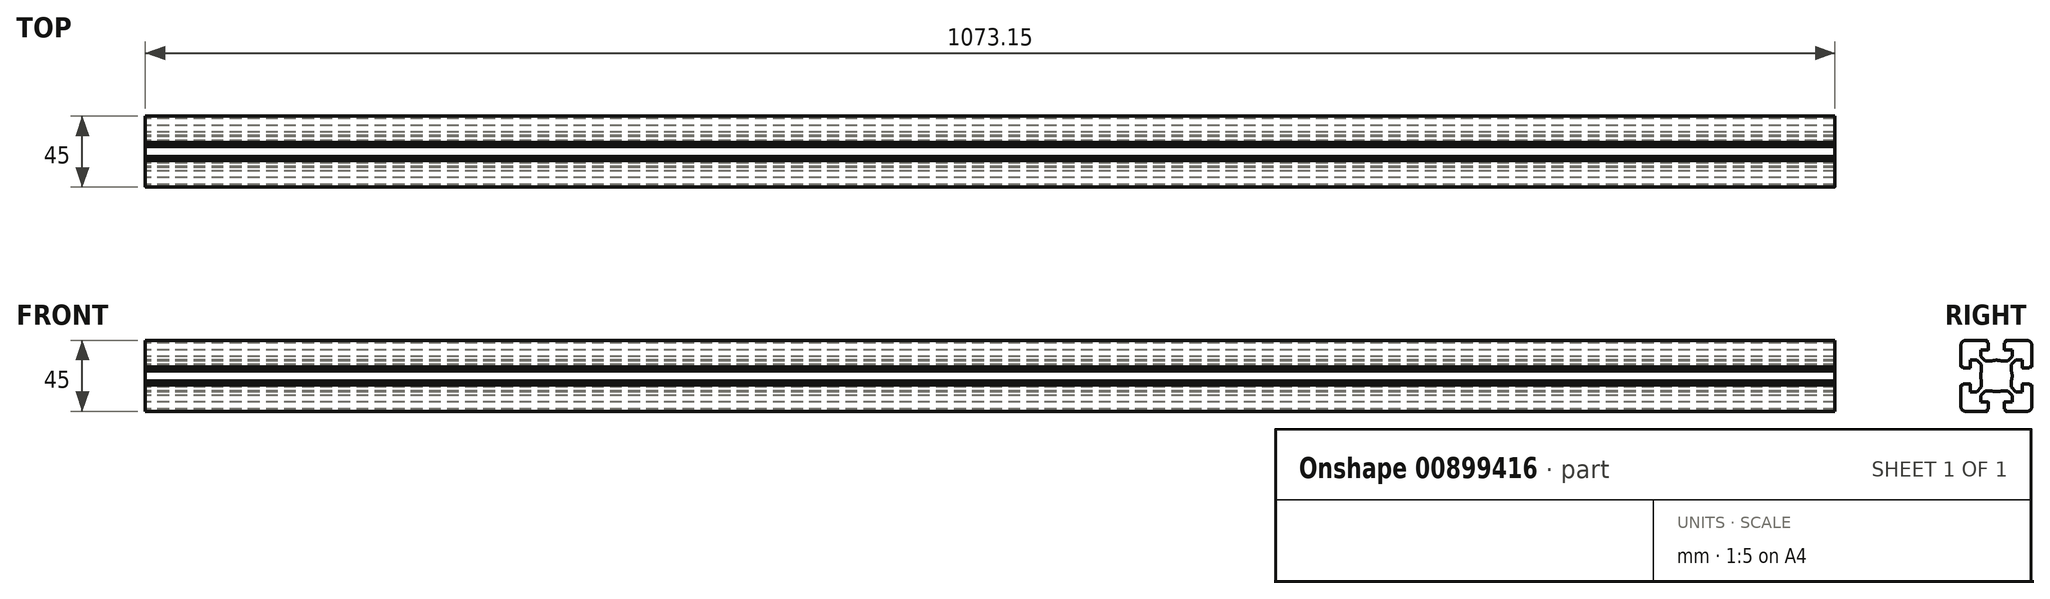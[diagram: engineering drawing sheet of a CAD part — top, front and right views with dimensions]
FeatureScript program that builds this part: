
annotation { "Feature Type Name" : "Feature", "Feature Type Description" : "" }
export const myFeature = defineFeature(function(context is Context, id is Id, definition is map)
    precondition{}
    {
        {
            var Q0;
            Q0=qCreatedBy(makeId("Right.planeOp"),FACE);
            var sketch = newSketch(context, id + "F0", { "sketchPlane" : qUnion([Q0])});
            skLineSegment(sketch, "E0", {"start": v(-20.09, -10.29) * mm, "end": v(-21.29, -10.29) * mm});
            skArc(sketch, "E1", {"start": v(-21.29, -10.29) * mm, "mid": v(-21.5, -10.38) * mm, "end": v(-21.59, -10.59) * mm});
            skLineSegment(sketch, "E2", {"start": v(-21.59, -10.59) * mm, "end": v(-21.59, -23.99) * mm});
            skArc(sketch, "E3", {"start": v(-21.59, -23.99) * mm, "mid": v(-20.7, -26.11) * mm, "end": v(-18.59, -26.99) * mm});
            skLineSegment(sketch, "E4", {"start": v(-18.59, -26.99) * mm, "end": v(-5.19, -26.99) * mm});
            skArc(sketch, "E5", {"start": v(-5.19, -26.99) * mm, "mid": v(-4.98, -26.9) * mm, "end": v(-4.89, -26.69) * mm});
            skLineSegment(sketch, "E6", {"start": v(-4.89, -26.69) * mm, "end": v(-4.89, -25.49) * mm});
            skLineSegment(sketch, "E7", {"start": v(-4.89, -25.49) * mm, "end": v(-4.39, -25.49) * mm});
            skArc(sketch, "E8", {"start": v(-4.39, -25.49) * mm, "mid": v(-4.18, -25.4) * mm, "end": v(-4.09, -25.19) * mm});
            skLineSegment(sketch, "E9", {"start": v(-4.09, -25.19) * mm, "end": v(-4.09, -21.29) * mm});
            skArc(sketch, "E10", {"start": v(-4.09, -21.29) * mm, "mid": v(-4.18, -21.08) * mm, "end": v(-4.39, -20.99) * mm});
            skLineSegment(sketch, "E11", {"start": v(-4.39, -20.99) * mm, "end": v(-9.14, -20.99) * mm});
            skLineSegment(sketch, "E12", {"start": v(-9.14, -20.99) * mm, "end": v(-9.14, -16.88) * mm});
            skLineSegment(sketch, "E13", {"start": v(-9.14, -16.88) * mm, "end": v(-6.25, -13.99) * mm});
            skLineSegment(sketch, "E14", {"start": v(-6.25, -13.99) * mm, "end": v(-2.21, -13.99) * mm});
            skArc(sketch, "E15", {"start": v(-2.21, -13.99) * mm, "mid": v(0.91, -14.49) * mm, "end": v(4.03, -13.99) * mm});
            skLineSegment(sketch, "E16", {"start": v(-20.09, -10.29) * mm, "end": v(-20.09, -9.79) * mm});
            skArc(sketch, "E17", {"start": v(-20.09, -9.79) * mm, "mid": v(-20, -9.58) * mm, "end": v(-19.79, -9.49) * mm});
            skLineSegment(sketch, "E18", {"start": v(-19.79, -9.49) * mm, "end": v(-15.89, -9.49) * mm});
            skArc(sketch, "E19", {"start": v(-15.89, -9.49) * mm, "mid": v(-15.68, -9.58) * mm, "end": v(-15.59, -9.79) * mm});
            skLineSegment(sketch, "E20", {"start": v(-15.59, -9.79) * mm, "end": v(-15.59, -14.54) * mm});
            skLineSegment(sketch, "E21", {"start": v(-15.59, -14.54) * mm, "end": v(-11.48, -14.54) * mm});
            skLineSegment(sketch, "E22", {"start": v(-11.48, -14.54) * mm, "end": v(-8.59, -11.65) * mm});
            skLineSegment(sketch, "E23", {"start": v(-8.59, -11.65) * mm, "end": v(-8.59, -7.61) * mm});
            skLineSegment(sketch, "E24", {"start": v(29.82, -4.49) * mm, "end": v(-31.05, -4.49) * mm});
            skLineSegment(sketch, "E25.MirrorCS", {"start": v(6.71, -25.49) * mm, "end": v(6.21, -25.49) * mm});
            skArc(sketch, "E26.MirrorCS", {"start": v(7.01, -26.99) * mm, "mid": v(6.8, -26.9) * mm, "end": v(6.71, -26.69) * mm});
            skLineSegment(sketch, "E27.MirrorCS", {"start": v(10.41, -11.65) * mm, "end": v(10.41, -7.61) * mm});
            skArc(sketch, "E28.MirrorCS", {"start": v(6.21, -25.49) * mm, "mid": v(6, -25.4) * mm, "end": v(5.91, -25.19) * mm});
            skLineSegment(sketch, "E29.MirrorCS", {"start": v(6.71, -26.69) * mm, "end": v(6.71, -25.49) * mm});
            skArc(sketch, "E30.MirrorCS", {"start": v(5.91, -21.29) * mm, "mid": v(6, -21.08) * mm, "end": v(6.21, -20.99) * mm});
            skLineSegment(sketch, "E31.MirrorCS", {"start": v(10.96, -16.88) * mm, "end": v(8.07, -13.99) * mm});
            skLineSegment(sketch, "E32.MirrorCS", {"start": v(13.3, -14.54) * mm, "end": v(10.41, -11.65) * mm});
            skLineSegment(sketch, "E33.MirrorCS", {"start": v(17.41, -14.54) * mm, "end": v(13.3, -14.54) * mm});
            skLineSegment(sketch, "E34.MirrorCS", {"start": v(17.41, -9.79) * mm, "end": v(17.41, -14.54) * mm});
            skLineSegment(sketch, "E35.MirrorCS", {"start": v(6.21, -20.99) * mm, "end": v(10.96, -20.99) * mm});
            skLineSegment(sketch, "E36.MirrorCS", {"start": v(8.07, -13.99) * mm, "end": v(4.03, -13.99) * mm});
            skArc(sketch, "E37.MirrorCS", {"start": v(4.03, -13.99) * mm, "mid": v(0.91, -14.49) * mm, "end": v(-2.21, -13.99) * mm});
            skLineSegment(sketch, "E38.MirrorCS", {"start": v(10.96, -20.99) * mm, "end": v(10.96, -16.88) * mm});
            skLineSegment(sketch, "E39.MirrorCS", {"start": v(5.91, -25.19) * mm, "end": v(5.91, -21.29) * mm});
            skArc(sketch, "E40.MirrorCS", {"start": v(23.41, -23.99) * mm, "mid": v(22.53, -26.11) * mm, "end": v(20.41, -26.99) * mm});
            skLineSegment(sketch, "E41.MirrorCS", {"start": v(20.41, -26.99) * mm, "end": v(7.01, -26.99) * mm});
            skLineSegment(sketch, "E42.MirrorCS", {"start": v(23.41, -10.59) * mm, "end": v(23.41, -23.99) * mm});
            skArc(sketch, "E43.MirrorCS", {"start": v(17.71, -9.49) * mm, "mid": v(17.5, -9.58) * mm, "end": v(17.41, -9.79) * mm});
            skArc(sketch, "E44.MirrorCS", {"start": v(23.11, -10.29) * mm, "mid": v(23.32, -10.38) * mm, "end": v(23.41, -10.59) * mm});
            skLineSegment(sketch, "E45.MirrorCS", {"start": v(21.91, -10.29) * mm, "end": v(21.91, -9.79) * mm});
            skLineSegment(sketch, "E46.MirrorCS", {"start": v(21.91, -10.29) * mm, "end": v(23.11, -10.29) * mm});
            skArc(sketch, "E47.MirrorCS", {"start": v(21.91, -9.79) * mm, "mid": v(21.82, -9.58) * mm, "end": v(21.61, -9.49) * mm});
            skLineSegment(sketch, "E48.MirrorCS", {"start": v(21.61, -9.49) * mm, "end": v(17.71, -9.49) * mm});
            skLineSegment(sketch, "E49.MirrorCS", {"start": v(6.71, 16.51) * mm, "end": v(6.21, 16.51) * mm});
            skArc(sketch, "E50.MirrorCS", {"start": v(-4.39, 16.51) * mm, "mid": v(-4.18, 16.42) * mm, "end": v(-4.09, 16.21) * mm});
            skLineSegment(sketch, "E51.MirrorCS", {"start": v(-4.89, 16.51) * mm, "end": v(-4.39, 16.51) * mm});
            skArc(sketch, "E52.MirrorCS", {"start": v(5.91, 12.31) * mm, "mid": v(6, 12.1) * mm, "end": v(6.21, 12.01) * mm});
            skLineSegment(sketch, "E53.MirrorCS", {"start": v(6.71, 17.71) * mm, "end": v(6.71, 16.51) * mm});
            skLineSegment(sketch, "E54.MirrorCS", {"start": v(-4.89, 17.71) * mm, "end": v(-4.89, 16.51) * mm});
            skArc(sketch, "E55.MirrorCS", {"start": v(-5.19, 18.01) * mm, "mid": v(-4.98, 17.92) * mm, "end": v(-4.89, 17.71) * mm});
            skArc(sketch, "E56.MirrorCS", {"start": v(-4.09, 12.31) * mm, "mid": v(-4.18, 12.1) * mm, "end": v(-4.39, 12.01) * mm});
            skArc(sketch, "E57.MirrorCS", {"start": v(7.01, 18.01) * mm, "mid": v(6.8, 17.92) * mm, "end": v(6.71, 17.71) * mm});
            skArc(sketch, "E58.MirrorCS", {"start": v(6.21, 16.51) * mm, "mid": v(6, 16.42) * mm, "end": v(5.91, 16.21) * mm});
            skArc(sketch, "E59.MirrorCS", {"start": v(23.11, 1.31) * mm, "mid": v(23.32, 1.4) * mm, "end": v(23.41, 1.61) * mm});
            skLineSegment(sketch, "E60.MirrorCS", {"start": v(21.91, 1.31) * mm, "end": v(21.91, 0.81) * mm});
            skArc(sketch, "E61.MirrorCS", {"start": v(-15.89, 0.51) * mm, "mid": v(-15.68, 0.6) * mm, "end": v(-15.59, 0.81) * mm});
            skArc(sketch, "E62.MirrorCS", {"start": v(-21.29, 1.31) * mm, "mid": v(-21.5, 1.4) * mm, "end": v(-21.59, 1.61) * mm});
            skArc(sketch, "E63.MirrorCS", {"start": v(17.71, 0.51) * mm, "mid": v(17.5, 0.6) * mm, "end": v(17.41, 0.81) * mm});
            skArc(sketch, "E64.MirrorCS", {"start": v(21.91, 0.81) * mm, "mid": v(21.82, 0.6) * mm, "end": v(21.61, 0.51) * mm});
            skLineSegment(sketch, "E65.MirrorCS", {"start": v(21.91, 1.31) * mm, "end": v(23.11, 1.31) * mm});
            skArc(sketch, "E66.MirrorCS", {"start": v(14.31, 5.31) * mm, "mid": v(14.1, 5.4) * mm, "end": v(14.01, 5.61) * mm});
            skArc(sketch, "E67.MirrorCS", {"start": v(-20.09, 0.81) * mm, "mid": v(-20, 0.6) * mm, "end": v(-19.79, 0.51) * mm});
            skLineSegment(sketch, "E68.MirrorCS", {"start": v(-20.09, 1.31) * mm, "end": v(-21.29, 1.31) * mm});
            skLineSegment(sketch, "E69.MirrorCS", {"start": v(-20.09, 1.31) * mm, "end": v(-20.09, 0.81) * mm});
            skLineSegment(sketch, "E70.MirrorCS", {"start": v(8.07, 5.01) * mm, "end": v(4.03, 5.01) * mm});
            skLineSegment(sketch, "E71.MirrorCS", {"start": v(-4.09, 16.21) * mm, "end": v(-4.09, 12.31) * mm});
            skLineSegment(sketch, "E72.MirrorCS", {"start": v(-9.14, 12.01) * mm, "end": v(-9.14, 7.9) * mm});
            skLineSegment(sketch, "E73.MirrorCS", {"start": v(-15.59, 5.56) * mm, "end": v(-11.48, 5.56) * mm});
            skLineSegment(sketch, "E74.MirrorCS", {"start": v(-4.39, 12.01) * mm, "end": v(-9.14, 12.01) * mm});
            skLineSegment(sketch, "E75.MirrorCS", {"start": v(-9.14, 7.9) * mm, "end": v(-6.25, 5.01) * mm});
            skLineSegment(sketch, "E76.MirrorCS", {"start": v(10.96, 12.01) * mm, "end": v(10.96, 7.9) * mm});
            skArc(sketch, "E77.MirrorCS", {"start": v(-21.59, 15.01) * mm, "mid": v(-20.7, 17.13) * mm, "end": v(-18.59, 18.01) * mm});
            skLineSegment(sketch, "E78.MirrorCS", {"start": v(23.41, 1.61) * mm, "end": v(23.41, 15.01) * mm});
            skLineSegment(sketch, "E79.MirrorCS", {"start": v(13.3, 5.56) * mm, "end": v(10.41, 2.67) * mm});
            skLineSegment(sketch, "E80.MirrorCS", {"start": v(-8.59, 2.67) * mm, "end": v(-8.59, -1.37) * mm});
            skLineSegment(sketch, "E81.MirrorCS", {"start": v(-15.59, 0.81) * mm, "end": v(-15.59, 5.56) * mm});
            skLineSegment(sketch, "E82.MirrorCS", {"start": v(10.41, 2.67) * mm, "end": v(10.41, -1.37) * mm});
            skLineSegment(sketch, "E83.MirrorCS", {"start": v(-18.59, 18.01) * mm, "end": v(-5.19, 18.01) * mm});
            skLineSegment(sketch, "E84.MirrorCS", {"start": v(10.96, 7.9) * mm, "end": v(8.07, 5.01) * mm});
            skLineSegment(sketch, "E85.MirrorCS", {"start": v(17.41, 5.56) * mm, "end": v(13.3, 5.56) * mm});
            skArc(sketch, "E86.MirrorCS", {"start": v(23.41, 15.01) * mm, "mid": v(22.53, 17.13) * mm, "end": v(20.41, 18.01) * mm});
            skLineSegment(sketch, "E87.MirrorCS", {"start": v(5.91, 16.21) * mm, "end": v(5.91, 12.31) * mm});
            skLineSegment(sketch, "E88.MirrorCS", {"start": v(17.41, 0.81) * mm, "end": v(17.41, 5.56) * mm});
            skLineSegment(sketch, "E89.MirrorCS", {"start": v(-11.48, 5.56) * mm, "end": v(-8.59, 2.67) * mm});
            skLineSegment(sketch, "E90.MirrorCS", {"start": v(-6.25, 5.01) * mm, "end": v(-2.21, 5.01) * mm});
            skLineSegment(sketch, "E91.MirrorCS", {"start": v(-21.59, 1.61) * mm, "end": v(-21.59, 15.01) * mm});
            skArc(sketch, "E92.MirrorCS", {"start": v(4.03, 5.01) * mm, "mid": v(0.91, 5.51) * mm, "end": v(-2.21, 5.01) * mm});
            skLineSegment(sketch, "E93.MirrorCS", {"start": v(6.21, 12.01) * mm, "end": v(10.96, 12.01) * mm});
            skArc(sketch, "E94.MirrorCS", {"start": v(-2.21, 5.01) * mm, "mid": v(0.91, 5.51) * mm, "end": v(4.03, 5.01) * mm});
            skLineSegment(sketch, "E95.MirrorCS", {"start": v(20.41, 18.01) * mm, "end": v(7.01, 18.01) * mm});
            skLineSegment(sketch, "E96.MirrorCS", {"start": v(-19.79, 0.51) * mm, "end": v(-15.89, 0.51) * mm});
            skLineSegment(sketch, "E97.MirrorCS", {"start": v(21.61, 0.51) * mm, "end": v(17.71, 0.51) * mm});
            skLineSegment(sketch, "E98.MirrorCS", {"start": v(0.91, -27.65) * mm, "end": v(0.91, 19.82) * mm});
            skArc(sketch, "E99", {"start": v(-8.59, -1.37) * mm, "mid": v(-9.09, -4.49) * mm, "end": v(-8.59, -7.61) * mm});
            skArc(sketch, "E100", {"start": v(10.41, -7.61) * mm, "mid": v(10.91, -4.49) * mm, "end": v(10.41, -1.37) * mm});
            skSolve(sketch);
        }
        {
            var Q0;
            Q0=qSketchRegion(id+"F0",true);
            extrude(context, id + "F1", {"entities" : qUnion([Q0]), "depth" : 1073.15 * mm, "offsetDistance" : 25.4 * mm});
        }
    });
